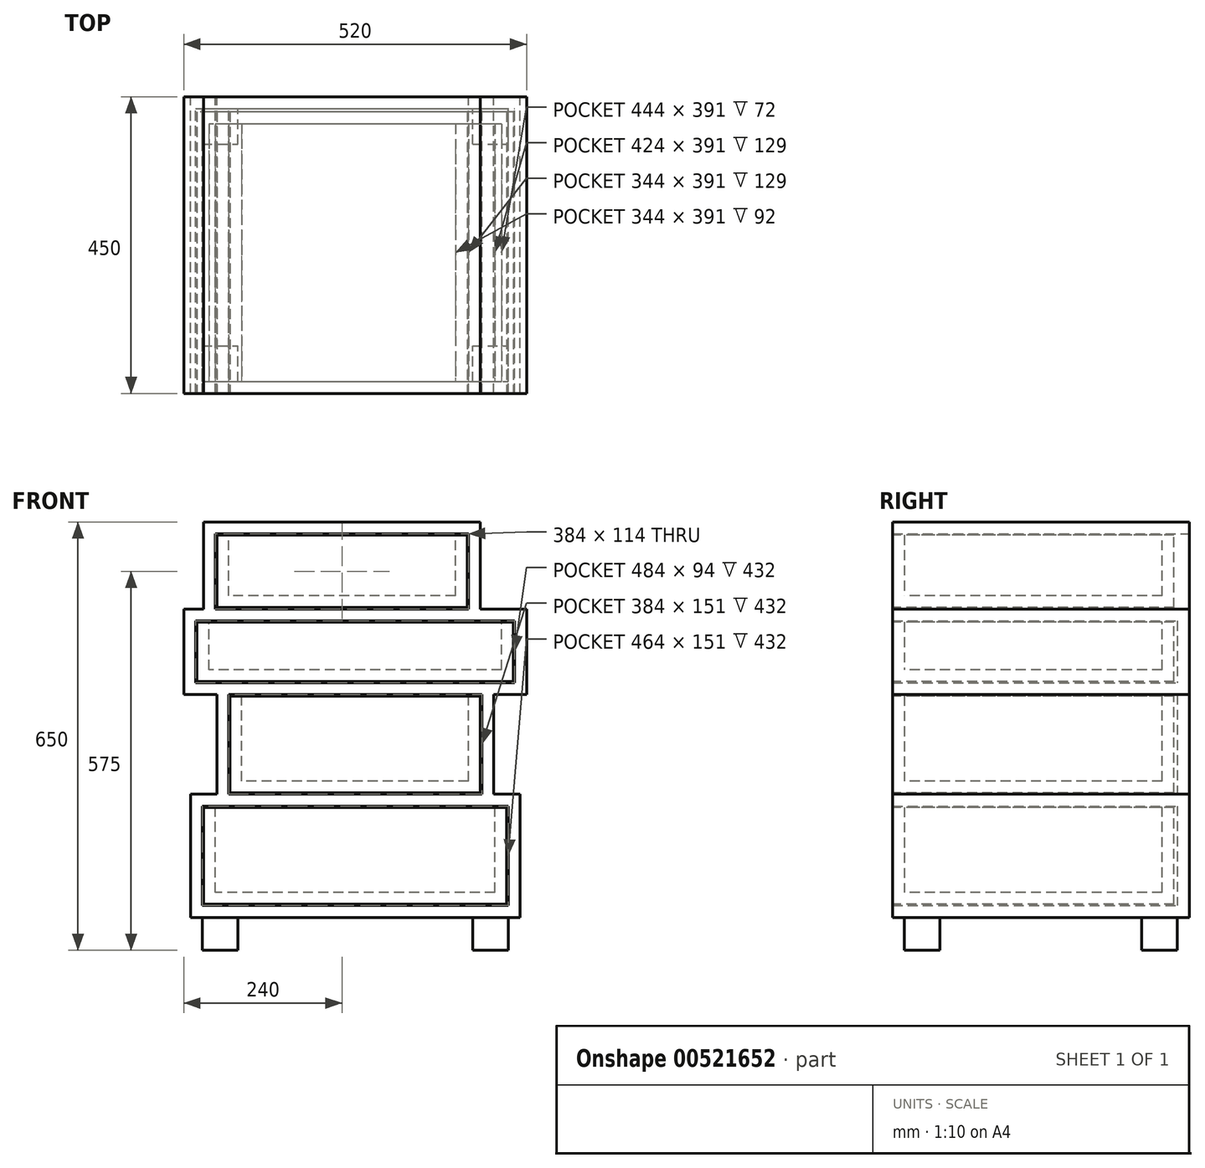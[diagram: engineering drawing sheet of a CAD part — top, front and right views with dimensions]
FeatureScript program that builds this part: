
annotation { "Feature Type Name" : "Feature", "Feature Type Description" : "" }
export const myFeature = defineFeature(function(context is Context, id is Id, definition is map)
    precondition{}
    {
        {
            var Q0;
            Q0=qCreatedBy(makeId("Front.planeOp"),FACE);
            var sketch = newSketch(context, id + "F0", { "sketchPlane" : qUnion([Q0])});
            skLineSegment(sketch, "E0", {"start": v(-192.99, -50) * mm, "end": v(31.49, -50) * mm, "construction": true});
            skLineSegment(sketch, "E1.bottom", {"start": v(-260, 468) * mm, "end": v(260, 468) * mm});
            skLineSegment(sketch, "E1.top", {"start": v(-260, 450) * mm, "end": v(260, 450) * mm});
            skLineSegment(sketch, "E1.left", {"start": v(-260, 468) * mm, "end": v(-260, 450) * mm});
            skLineSegment(sketch, "E1.right", {"start": v(260, 468) * mm, "end": v(260, 450) * mm});
            skLineSegment(sketch, "E2.bottom", {"start": v(-250, 187) * mm, "end": v(250, 187) * mm});
            skLineSegment(sketch, "E2.top", {"start": v(-250, 169) * mm, "end": v(250, 169) * mm});
            skLineSegment(sketch, "E2.left", {"start": v(-250, 187) * mm, "end": v(-250, 169) * mm});
            skLineSegment(sketch, "E2.right", {"start": v(250, 187) * mm, "end": v(250, 169) * mm});
            skLineSegment(sketch, "E3.bottom", {"start": v(-250, 18) * mm, "end": v(250, 18) * mm});
            skLineSegment(sketch, "E3.top", {"start": v(-250, 0) * mm, "end": v(250, 0) * mm});
            skLineSegment(sketch, "E3.left", {"start": v(-250, 18) * mm, "end": v(-250, 0) * mm});
            skLineSegment(sketch, "E3.right", {"start": v(250, 18) * mm, "end": v(250, 0) * mm});
            skLineSegment(sketch, "E4.bottom", {"start": v(-260, 356) * mm, "end": v(260, 356) * mm});
            skLineSegment(sketch, "E4.top", {"start": v(-260, 338) * mm, "end": v(260, 338) * mm});
            skLineSegment(sketch, "E4.left", {"start": v(-260, 356) * mm, "end": v(-260, 338) * mm});
            skLineSegment(sketch, "E4.right", {"start": v(260, 356) * mm, "end": v(260, 338) * mm});
            skLineSegment(sketch, "E5.bottom", {"start": v(-250, 169) * mm, "end": v(-232, 169) * mm});
            skLineSegment(sketch, "E5.top", {"start": v(-250, 18) * mm, "end": v(-232, 18) * mm});
            skLineSegment(sketch, "E5.left", {"start": v(-250, 169) * mm, "end": v(-250, 18) * mm});
            skLineSegment(sketch, "E5.right", {"start": v(-232, 169) * mm, "end": v(-232, 18) * mm});
            skLineSegment(sketch, "E6.bottom", {"start": v(232, 169) * mm, "end": v(250, 169) * mm});
            skLineSegment(sketch, "E6.top", {"start": v(232, 18) * mm, "end": v(250, 18) * mm});
            skLineSegment(sketch, "E6.left", {"start": v(232, 169) * mm, "end": v(232, 18) * mm});
            skLineSegment(sketch, "E6.right", {"start": v(250, 169) * mm, "end": v(250, 18) * mm});
            skLineSegment(sketch, "E7.bottom", {"start": v(192, 338) * mm, "end": v(210, 338) * mm});
            skLineSegment(sketch, "E7.top", {"start": v(192, 187) * mm, "end": v(210, 187) * mm});
            skLineSegment(sketch, "E7.left", {"start": v(192, 338) * mm, "end": v(192, 187) * mm});
            skLineSegment(sketch, "E7.right", {"start": v(210, 338) * mm, "end": v(210, 187) * mm});
            skLineSegment(sketch, "E8.bottom", {"start": v(-210, 338) * mm, "end": v(-192, 338) * mm});
            skLineSegment(sketch, "E8.top", {"start": v(-210, 187) * mm, "end": v(-192, 187) * mm});
            skLineSegment(sketch, "E8.left", {"start": v(-210, 338) * mm, "end": v(-210, 187) * mm});
            skLineSegment(sketch, "E8.right", {"start": v(-192, 338) * mm, "end": v(-192, 187) * mm});
            skLineSegment(sketch, "E9.bottom", {"start": v(-260, 450) * mm, "end": v(-242, 450) * mm});
            skLineSegment(sketch, "E9.top", {"start": v(-260, 356) * mm, "end": v(-242, 356) * mm});
            skLineSegment(sketch, "E9.left", {"start": v(-260, 450) * mm, "end": v(-260, 356) * mm});
            skLineSegment(sketch, "E9.right", {"start": v(-242, 450) * mm, "end": v(-242, 356) * mm});
            skLineSegment(sketch, "E10.bottom", {"start": v(260, 450) * mm, "end": v(242, 450) * mm});
            skLineSegment(sketch, "E10.top", {"start": v(260, 356) * mm, "end": v(242, 356) * mm});
            skLineSegment(sketch, "E10.left", {"start": v(260, 450) * mm, "end": v(260, 356) * mm});
            skLineSegment(sketch, "E10.right", {"start": v(242, 450) * mm, "end": v(242, 356) * mm});
            skLineSegment(sketch, "E11.bottom", {"start": v(-230, 582) * mm, "end": v(-212, 582) * mm});
            skLineSegment(sketch, "E11.top", {"start": v(-230, 468) * mm, "end": v(-212, 468) * mm});
            skLineSegment(sketch, "E11.left", {"start": v(-230, 582) * mm, "end": v(-230, 468) * mm});
            skLineSegment(sketch, "E11.right", {"start": v(-212, 582) * mm, "end": v(-212, 468) * mm});
            skLineSegment(sketch, "E12.bottom", {"start": v(172, 582) * mm, "end": v(190, 582) * mm});
            skLineSegment(sketch, "E12.top", {"start": v(172, 468) * mm, "end": v(190, 468) * mm});
            skLineSegment(sketch, "E12.left", {"start": v(172, 582) * mm, "end": v(172, 468) * mm});
            skLineSegment(sketch, "E12.right", {"start": v(190, 582) * mm, "end": v(190, 468) * mm});
            skLineSegment(sketch, "E13.bottom", {"start": v(-230, 582) * mm, "end": v(190, 582) * mm});
            skLineSegment(sketch, "E13.top", {"start": v(-230, 600) * mm, "end": v(190, 600) * mm});
            skLineSegment(sketch, "E13.left", {"start": v(-230, 582) * mm, "end": v(-230, 600) * mm});
            skLineSegment(sketch, "E13.right", {"start": v(190, 582) * mm, "end": v(190, 600) * mm});
            skSolve(sketch);
        }
        {
            var Q0;
            Q0 = qSketchRegion(id + "F0", true);
            extrude(context, id + "F1", {"entities" : qUnion([Q0]), "depth" : 450 * mm, "offsetDistance" : 25 * mm});
        }
        {
            var Q0;
            Q0=makeQuery(id+"F0.imprint","IMPRINT",FACE,{"disambiguationData":[TD([[makeQuery(id+"F0.imprint","IMPRINT",EDGE,{"derivedFrom":sQuery(id+"F0.wireOp",EDGE,"E1.top")}),-1.0]])]});
            var Q1;
            {var subQ0=sQuery(id+"F0.wireOp",EDGE,"E7.left");Q1=makeQuery(id+"F0.imprint","IMPRINT",FACE,{"disambiguationData":[TD([[makeQuery(id+"F0.imprint","IMPRINT",EDGE,{"derivedFrom":subQ0}),-1.0]])]});}
            var Q2;
            Q2=makeQuery(id+"F0.imprint","IMPRINT",FACE,{"disambiguationData":[TD([[makeQuery(id+"F0.imprint","IMPRINT",EDGE,{"derivedFrom":sQuery(id+"F0.wireOp",EDGE,"E3.bottom")}),1.0]])]});
            extrude(context, id + "F2", {"entities" : qUnion([Q0, Q1, Q2]), "operationType" : NewBodyOperationType.ADD, "depth" : 18 * mm, "offsetDistance" : 25 * mm});
        }
        {
            var Q0;
            Q0=makeQuery(id+"F1.opExtrude","CAP_FACE",FACE,{"disambiguationData":[OSD([sQuery(id+"F0.wireOp",EDGE,"E1.bottom"),sQuery(id+"F0.wireOp",EDGE,"E1.top"),sQuery(id+"F0.wireOp",EDGE,"E1.left"),sQuery(id+"F0.wireOp",EDGE,"E1.right"),sQuery(id+"F0.wireOp",EDGE,"E2.bottom"),sQuery(id+"F0.wireOp",EDGE,"E2.top"),sQuery(id+"F0.wireOp",EDGE,"E2.left"),sQuery(id+"F0.wireOp",EDGE,"E2.right"),sQuery(id+"F0.wireOp",EDGE,"E3.bottom"),sQuery(id+"F0.wireOp",EDGE,"E3.top"),sQuery(id+"F0.wireOp",EDGE,"E3.left"),sQuery(id+"F0.wireOp",EDGE,"E3.right"),sQuery(id+"F0.wireOp",EDGE,"E4.bottom"),sQuery(id+"F0.wireOp",EDGE,"E4.top"),sQuery(id+"F0.wireOp",EDGE,"E4.left"),sQuery(id+"F0.wireOp",EDGE,"E4.right"),sQuery(id+"F0.wireOp",EDGE,"E5.left"),sQuery(id+"F0.wireOp",EDGE,"E5.right"),sQuery(id+"F0.wireOp",EDGE,"E6.left"),sQuery(id+"F0.wireOp",EDGE,"E6.right"),sQuery(id+"F0.wireOp",EDGE,"E7.left"),sQuery(id+"F0.wireOp",EDGE,"E7.right"),sQuery(id+"F0.wireOp",EDGE,"E8.left"),sQuery(id+"F0.wireOp",EDGE,"E8.right"),sQuery(id+"F0.wireOp",EDGE,"E9.left"),sQuery(id+"F0.wireOp",EDGE,"E9.right"),sQuery(id+"F0.wireOp",EDGE,"E10.left"),sQuery(id+"F0.wireOp",EDGE,"E10.right")])],"isStart":false});
            var sketch = newSketch(context, id + "F3", { "sketchPlane" : qUnion([Q0])});
            skLineSegment(sketch, "E14.0", {"start": v(-242, 450) * mm, "end": v(242, 450) * mm});
            skLineSegment(sketch, "E15.0", {"start": v(-242, 450) * mm, "end": v(-242, 356) * mm});
            skLineSegment(sketch, "E16.0", {"start": v(-242, 356) * mm, "end": v(242, 356) * mm});
            skLineSegment(sketch, "E17.0", {"start": v(242, 450) * mm, "end": v(242, 356) * mm});
            skLineSegment(sketch, "E18.0", {"start": v(-192, 338) * mm, "end": v(192, 338) * mm});
            skLineSegment(sketch, "E19.0", {"start": v(-192, 338) * mm, "end": v(-192, 187) * mm});
            skLineSegment(sketch, "E20.0", {"start": v(-192, 187) * mm, "end": v(192, 187) * mm});
            skLineSegment(sketch, "E21.0", {"start": v(192, 338) * mm, "end": v(192, 187) * mm});
            skLineSegment(sketch, "E22.0", {"start": v(232, 169) * mm, "end": v(232, 18) * mm});
            skLineSegment(sketch, "E23.0", {"start": v(-232, 169) * mm, "end": v(-232, 18) * mm});
            skLineSegment(sketch, "E24.0", {"start": v(-232, 169) * mm, "end": v(232, 169) * mm});
            skLineSegment(sketch, "E25.0", {"start": v(-232, 18) * mm, "end": v(232, 18) * mm});
            skLineSegment(sketch, "E26.bottom", {"start": v(-240, 448) * mm, "end": v(240, 448) * mm});
            skLineSegment(sketch, "E26.top", {"start": v(-240, 358) * mm, "end": v(240, 358) * mm});
            skLineSegment(sketch, "E26.left", {"start": v(-240, 448) * mm, "end": v(-240, 358) * mm});
            skLineSegment(sketch, "E26.right", {"start": v(240, 448) * mm, "end": v(240, 358) * mm});
            skLineSegment(sketch, "E27.bottom", {"start": v(-190, 336) * mm, "end": v(190, 336) * mm});
            skLineSegment(sketch, "E27.top", {"start": v(-190, 189) * mm, "end": v(190, 189) * mm});
            skLineSegment(sketch, "E27.left", {"start": v(-190, 336) * mm, "end": v(-190, 189) * mm});
            skLineSegment(sketch, "E27.right", {"start": v(190, 336) * mm, "end": v(190, 189) * mm});
            skLineSegment(sketch, "E28.bottom", {"start": v(-230, 167) * mm, "end": v(230, 167) * mm});
            skLineSegment(sketch, "E28.top", {"start": v(-230, 20) * mm, "end": v(230, 20) * mm});
            skLineSegment(sketch, "E28.left", {"start": v(-230, 167) * mm, "end": v(-230, 20) * mm});
            skLineSegment(sketch, "E28.right", {"start": v(230, 167) * mm, "end": v(230, 20) * mm});
            skLineSegment(sketch, "E29.0", {"start": v(-212, 582) * mm, "end": v(172, 582) * mm});
            skLineSegment(sketch, "E30.0", {"start": v(-230, 468) * mm, "end": v(-230, 468) * mm});
            skLineSegment(sketch, "E31.0.0", {"start": v(-212, 468) * mm, "end": v(-212, 582) * mm});
            skLineSegment(sketch, "E31.0.2", {"start": v(-212, 582) * mm, "end": v(-212, 468) * mm});
            skLineSegment(sketch, "E32.0.0", {"start": v(172, 582) * mm, "end": v(172, 468) * mm});
            skLineSegment(sketch, "E32.0.2", {"start": v(172, 468) * mm, "end": v(172, 582) * mm});
            skLineSegment(sketch, "E33.bottom", {"start": v(-210, 580) * mm, "end": v(170, 580) * mm});
            skLineSegment(sketch, "E33.top", {"start": v(-210, 470) * mm, "end": v(170, 470) * mm});
            skLineSegment(sketch, "E33.left", {"start": v(-210, 580) * mm, "end": v(-210, 470) * mm});
            skLineSegment(sketch, "E33.right", {"start": v(170, 580) * mm, "end": v(170, 470) * mm});
            skSolve(sketch);
        }
        {
            var Q0;
            Q0=makeQuery(id+"F3.imprint","IMPRINT",FACE,{"disambiguationData":[TD([[makeQuery(id+"F3.imprint","IMPRINT",EDGE,{"derivedFrom":sQuery(id+"F3.wireOp",EDGE,"E26.bottom")}),-1.0]])]});
            var Q1;
            Q1=makeQuery(id+"F3.imprint","IMPRINT",FACE,{"disambiguationData":[TD([[makeQuery(id+"F3.imprint","IMPRINT",EDGE,{"derivedFrom":sQuery(id+"F3.wireOp",EDGE,"E27.bottom")}),-1.0]])]});
            var Q2;
            Q2=makeQuery(id+"F3.imprint","IMPRINT",FACE,{"disambiguationData":[TD([[makeQuery(id+"F3.imprint","IMPRINT",EDGE,{"derivedFrom":sQuery(id+"F3.wireOp",EDGE,"E28.bottom")}),-1.0]])]});
            var Q3;
            Q3=makeQuery(id+"F3.imprint","IMPRINT",FACE,{"disambiguationData":[TD([[makeQuery(id+"F3.imprint","IMPRINT",EDGE,{"derivedFrom":sQuery(id+"F3.wireOp",EDGE,"E33.bottom")}),-1.0]])]});
            var Q4;
            Q4=makeQuery(id+"F2.opExtrude","CAP_FACE",FACE,{"disambiguationData":[OSD([sQuery(id+"F0.wireOp",EDGE,"E2.top"),sQuery(id+"F0.wireOp",EDGE,"E3.bottom"),sQuery(id+"F0.wireOp",EDGE,"E5.right"),sQuery(id+"F0.wireOp",EDGE,"E6.left")])],"isStart":false});
            extrude(context, id + "F4", {"entities" : qUnion([Q0, Q1, Q2, Q3]), "endBound" : BoundingType.UP_TO_SURFACE, "oppositeDirection" : true, "depth" : 25 * mm, "endBoundEntityFace" : qUnion([Q4]), "hasOffset" : true, "offsetDistance" : 5 * mm});
        }
        {
            var Q0;
            Q0=makeQuery(id+"F4.opExtrude","SWEPT_FACE",FACE,{"disambiguationData":[OSD([sQuery(id+"F3.wireOp",EDGE,"E26.bottom")])]});
            shell(context, id + "F5", {"entities" : qUnion([Q0]), "thickness" : 18 * mm});
        }
        {
            var Q0;
            Q0=makeQuery(id+"F4.opExtrude","SWEPT_FACE",FACE,{"disambiguationData":[OSD([sQuery(id+"F3.wireOp",EDGE,"E27.bottom")])]});
            shell(context, id + "F6", {"entities" : qUnion([Q0]), "thickness" : 18 * mm});
        }
        {
            var Q0;
            Q0=makeQuery(id+"F4.opExtrude","SWEPT_FACE",FACE,{"disambiguationData":[OSD([sQuery(id+"F3.wireOp",EDGE,"E28.bottom")])]});
            shell(context, id + "F7", {"entities" : qUnion([Q0]), "thickness" : 18 * mm});
        }
        {
            var Q0;
            Q0=makeQuery(id+"F1.opExtrude","SWEPT_FACE",FACE,{"disambiguationData":[OSD([sQuery(id+"F0.wireOp",EDGE,"E3.top")])]});
            var sketch = newSketch(context, id + "F8", { "sketchPlane" : qUnion([Q0])});
            skLineSegment(sketch, "E34.0", {"start": v(-250, 450) * mm, "end": v(250, 450) * mm});
            skLineSegment(sketch, "E35.0", {"start": v(-250, 450) * mm, "end": v(-250, 0) * mm});
            skLineSegment(sketch, "E36.0", {"start": v(-250, 0) * mm, "end": v(250, 0) * mm});
            skLineSegment(sketch, "E37.0", {"start": v(250, 450) * mm, "end": v(250, 0) * mm});
            skLineSegment(sketch, "E38.bottom", {"start": v(-232, 432) * mm, "end": v(-178, 432) * mm});
            skLineSegment(sketch, "E38.top", {"start": v(-232, 378) * mm, "end": v(-178, 378) * mm});
            skLineSegment(sketch, "E38.left", {"start": v(-232, 432) * mm, "end": v(-232, 378) * mm});
            skLineSegment(sketch, "E38.right", {"start": v(-178, 432) * mm, "end": v(-178, 378) * mm});
            skLineSegment(sketch, "E39.bottom", {"start": v(178, 432) * mm, "end": v(232, 432) * mm});
            skLineSegment(sketch, "E39.top", {"start": v(178, 378) * mm, "end": v(232, 378) * mm});
            skLineSegment(sketch, "E39.left", {"start": v(178, 432) * mm, "end": v(178, 378) * mm});
            skLineSegment(sketch, "E39.right", {"start": v(232, 432) * mm, "end": v(232, 378) * mm});
            skLineSegment(sketch, "E40.bottom", {"start": v(-232, 72) * mm, "end": v(-178, 72) * mm});
            skLineSegment(sketch, "E40.top", {"start": v(-232, 18) * mm, "end": v(-178, 18) * mm});
            skLineSegment(sketch, "E40.left", {"start": v(-232, 72) * mm, "end": v(-232, 18) * mm});
            skLineSegment(sketch, "E40.right", {"start": v(-178, 72) * mm, "end": v(-178, 18) * mm});
            skLineSegment(sketch, "E41.bottom", {"start": v(178, 72) * mm, "end": v(232, 72) * mm});
            skLineSegment(sketch, "E41.top", {"start": v(178, 18) * mm, "end": v(232, 18) * mm});
            skLineSegment(sketch, "E41.left", {"start": v(178, 72) * mm, "end": v(178, 18) * mm});
            skLineSegment(sketch, "E41.right", {"start": v(232, 72) * mm, "end": v(232, 18) * mm});
            skSolve(sketch);
        }
        {
            var Q0;
            Q0=makeQuery(id+"F8.imprint","IMPRINT",FACE,{"disambiguationData":[TD([[makeQuery(id+"F8.imprint","IMPRINT",EDGE,{"derivedFrom":sQuery(id+"F8.wireOp",EDGE,"E38.bottom")}),-1.0]])]});
            var Q1;
            Q1=makeQuery(id+"F8.imprint","IMPRINT",FACE,{"disambiguationData":[TD([[makeQuery(id+"F8.imprint","IMPRINT",EDGE,{"derivedFrom":sQuery(id+"F8.wireOp",EDGE,"E39.bottom")}),-1.0]])]});
            var Q2;
            Q2=makeQuery(id+"F8.imprint","IMPRINT",FACE,{"disambiguationData":[TD([[makeQuery(id+"F8.imprint","IMPRINT",EDGE,{"derivedFrom":sQuery(id+"F8.wireOp",EDGE,"E40.bottom")}),-1.0]])]});
            var Q3;
            Q3=makeQuery(id+"F8.imprint","IMPRINT",FACE,{"disambiguationData":[TD([[makeQuery(id+"F8.imprint","IMPRINT",EDGE,{"derivedFrom":sQuery(id+"F8.wireOp",EDGE,"E41.bottom")}),-1.0]])]});
            extrude(context, id + "F9", {"entities" : qUnion([Q0, Q1, Q2, Q3]), "operationType" : NewBodyOperationType.ADD, "depth" : 50 * mm, "offsetDistance" : 25 * mm});
        }
        {
            var Q0;
            Q0=makeQuery(id+"F4.opExtrude","SWEPT_FACE",FACE,{"disambiguationData":[OSD([sQuery(id+"F3.wireOp",EDGE,"E33.bottom")])]});
            shell(context, id + "F10", {"entities" : qUnion([Q0]), "thickness" : 18 * mm});
        }
    });
